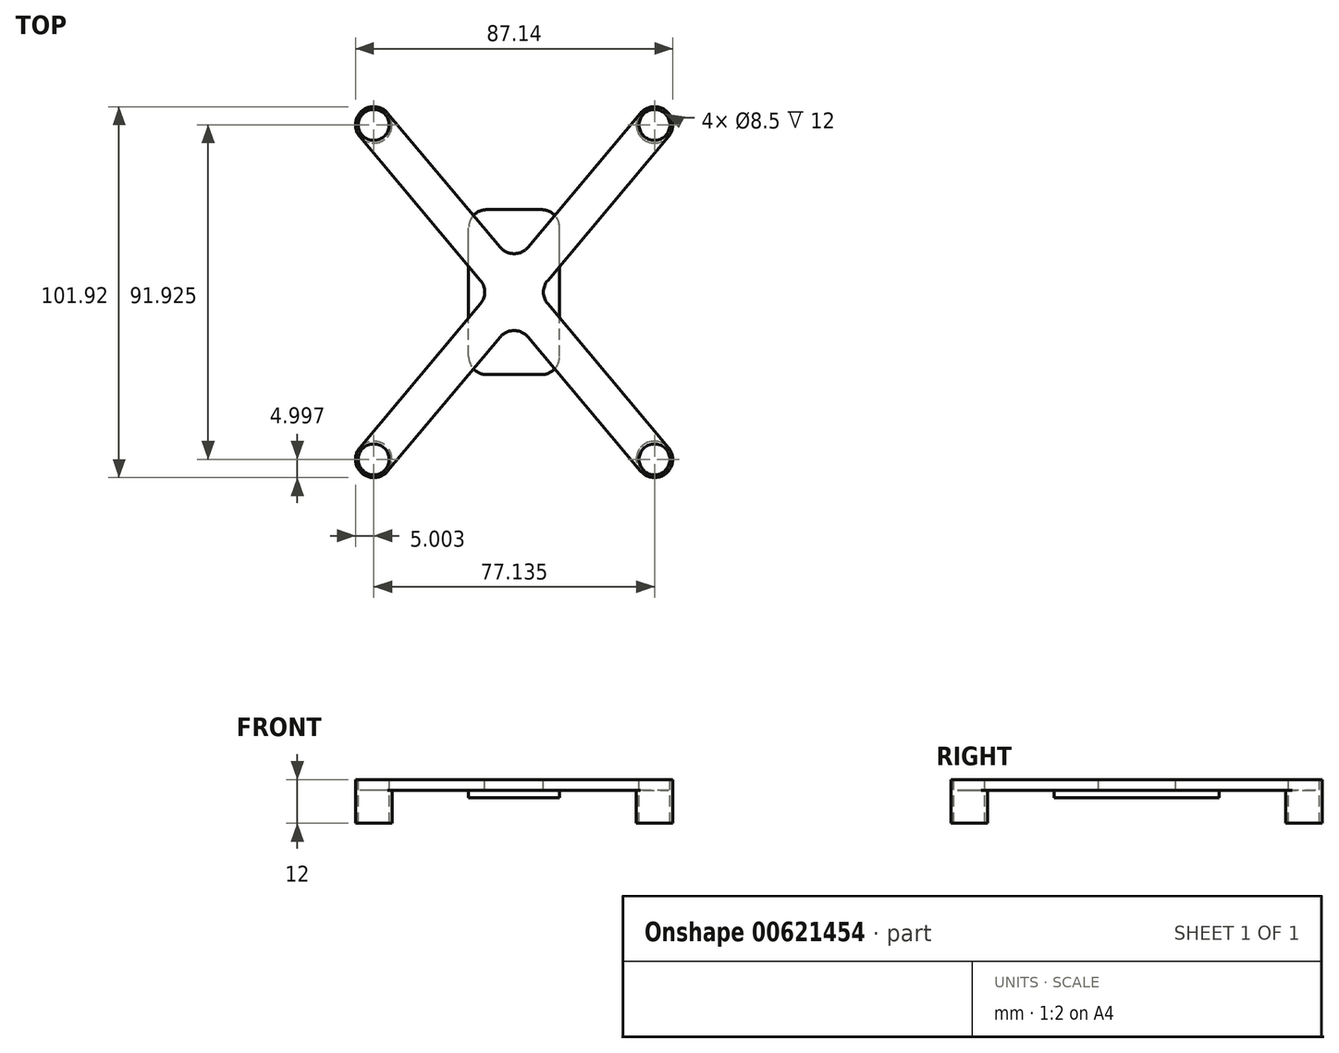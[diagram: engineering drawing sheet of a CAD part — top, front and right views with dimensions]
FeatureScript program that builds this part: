
annotation { "Feature Type Name" : "Feature", "Feature Type Description" : "" }
export const myFeature = defineFeature(function(context is Context, id is Id, definition is map)
    precondition{}
    {
        {
            var Q0;
            Q0=qCreatedBy(makeId("Top.planeOp"),FACE);
            var sketch = newSketch(context, id + "F0", { "sketchPlane" : qUnion([Q0])});
            skLineSegment(sketch, "E0.bottom", {"start": v(-42.4, 42.75) * mm, "end": v(-34.74, 49.18) * mm});
            skLineSegment(sketch, "E0.top", {"start": v(34.74, -49.18) * mm, "end": v(42.4, -42.75) * mm});
            skLineSegment(sketch, "E0.left", {"start": v(-42.4, 42.75) * mm, "end": v(-6.53, 0) * mm});
            skLineSegment(sketch, "E0.right", {"start": v(-34.74, 49.18) * mm, "end": v(0, 7.78) * mm});
            skPoint(sketch, "E0.middle", {"position": v(0, 0) * mm});
            skLineSegment(sketch, "E1.bottom", {"start": v(42.4, 42.75) * mm, "end": v(34.74, 49.18) * mm});
            skLineSegment(sketch, "E1.top", {"start": v(-34.74, -49.18) * mm, "end": v(-42.4, -42.75) * mm});
            skLineSegment(sketch, "E1.left", {"start": v(42.4, 42.75) * mm, "end": v(6.53, 0) * mm});
            skLineSegment(sketch, "E1.right", {"start": v(34.74, 49.18) * mm, "end": v(0, 7.78) * mm});
            skLineSegment(sketch, "E2.trimOffspring", {"start": v(-6.53, 0) * mm, "end": v(-42.4, -42.75) * mm});
            skLineSegment(sketch, "E3.trimOffspring", {"start": v(0, -7.78) * mm, "end": v(34.74, -49.18) * mm});
            skLineSegment(sketch, "E4.trimOffspring", {"start": v(0, -7.78) * mm, "end": v(-34.74, -49.18) * mm});
            skLineSegment(sketch, "E5.trimOffspring", {"start": v(6.53, 0) * mm, "end": v(42.4, -42.75) * mm});
            skSolve(sketch);
        }
        {
            var Q0;
            Q0=makeQuery(id+"F0.imprint","IMPRINT",FACE,{"disambiguationData":[TD([[makeQuery(id+"F0.imprint","IMPRINT",EDGE,{"derivedFrom":sQuery(id+"F0.wireOp",EDGE,"E0.bottom")}),-1.0]])]});
            extrude(context, id + "F1", {"entities" : qUnion([Q0]), "depth" : 3 * mm, "offsetDistance" : 25 * mm});
        }
        {
            var Q0;
            Q0=makeQuery(id+"F1.opExtrude","CAP_FACE",FACE,{"disambiguationData":[OSD([sQuery(id+"F0.wireOp",EDGE,"E0.bottom"),sQuery(id+"F0.wireOp",EDGE,"E0.top"),sQuery(id+"F0.wireOp",EDGE,"E0.left"),sQuery(id+"F0.wireOp",EDGE,"E0.right"),sQuery(id+"F0.wireOp",EDGE,"E1.bottom"),sQuery(id+"F0.wireOp",EDGE,"E1.top"),sQuery(id+"F0.wireOp",EDGE,"E1.left"),sQuery(id+"F0.wireOp",EDGE,"E1.right"),sQuery(id+"F0.wireOp",EDGE,"E2.trimOffspring"),sQuery(id+"F0.wireOp",EDGE,"E3.trimOffspring"),sQuery(id+"F0.wireOp",EDGE,"E4.trimOffspring"),sQuery(id+"F0.wireOp",EDGE,"E5.trimOffspring")])],"isStart":false});
            var sketch = newSketch(context, id + "F2", { "sketchPlane" : qUnion([Q0])});
            skCircle(sketch, "E6", {"center": v(-38.57, 45.96) * mm, "radius": 4.25 * mm});
            skCircle(sketch, "E7", {"center": v(-38.57, 45.96) * mm, "radius": 5 * mm});
            skCircle(sketch, "E8", {"center": v(38.57, 45.96) * mm, "radius": 5 * mm});
            skCircle(sketch, "E9", {"center": v(38.57, 45.96) * mm, "radius": 4.25 * mm});
            skCircle(sketch, "E10", {"center": v(38.57, -45.96) * mm, "radius": 5 * mm});
            skCircle(sketch, "E11", {"center": v(38.57, -45.96) * mm, "radius": 4.25 * mm});
            skCircle(sketch, "E12", {"center": v(-38.57, -45.96) * mm, "radius": 5 * mm});
            skCircle(sketch, "E13", {"center": v(-38.57, -45.96) * mm, "radius": 4.25 * mm});
            skSolve(sketch);
        }
        {
            var Q0;
            {var subQ1=makeQuery(id+"F1.opExtrude","CAP_EDGE",EDGE,{"disambiguationData":[OSD([sQuery(id+"F0.wireOp",EDGE,"E1.top")])],"isStart":false});var subQ4=sQuery(id+"F2.wireOp",EDGE,"E13");var subQ5=makeQuery(id+"F2.imprint","INTERSECT",VERTEX,{"disambiguationData":[OD(0.0)],"derivedFrom":[subQ1,subQ4]});Q0=makeQuery(id+"F2.imprint","IMPRINT",FACE,{"disambiguationData":[TD([[makeQuery(id+"F2.imprint","IMPRINT",EDGE,{"disambiguationData":[TD([[subQ5,1.0]])],"derivedFrom":subQ4}),-1.0]])]});}
            var Q1;
            {var subQ1=makeQuery(id+"F1.opExtrude","CAP_EDGE",EDGE,{"disambiguationData":[OSD([sQuery(id+"F0.wireOp",EDGE,"E1.top")])],"isStart":false});var subQ4=sQuery(id+"F2.wireOp",EDGE,"E13");var subQ5=makeQuery(id+"F2.imprint","INTERSECT",VERTEX,{"disambiguationData":[OD(0.0)],"derivedFrom":[subQ1,subQ4]});Q1=makeQuery(id+"F2.imprint","IMPRINT",FACE,{"disambiguationData":[TD([[makeQuery(id+"F2.imprint","IMPRINT",EDGE,{"disambiguationData":[TD([[subQ5,-1.0]])],"derivedFrom":subQ4}),-1.0]])]});}
            var Q2;
            {var subQ1=makeQuery(id+"F1.opExtrude","CAP_EDGE",EDGE,{"disambiguationData":[OSD([sQuery(id+"F0.wireOp",EDGE,"E0.top")])],"isStart":false});var subQ4=sQuery(id+"F2.wireOp",EDGE,"E11");var subQ5=makeQuery(id+"F2.imprint","INTERSECT",VERTEX,{"disambiguationData":[OD(0.0)],"derivedFrom":[subQ1,subQ4]});Q2=makeQuery(id+"F2.imprint","IMPRINT",FACE,{"disambiguationData":[TD([[makeQuery(id+"F2.imprint","IMPRINT",EDGE,{"disambiguationData":[TD([[subQ5,-1.0]])],"derivedFrom":subQ4}),-1.0]])]});}
            var Q3;
            {var subQ1=makeQuery(id+"F1.opExtrude","CAP_EDGE",EDGE,{"disambiguationData":[OSD([sQuery(id+"F0.wireOp",EDGE,"E0.top")])],"isStart":false});var subQ4=sQuery(id+"F2.wireOp",EDGE,"E11");var subQ6=makeQuery(id+"F2.imprint","INTERSECT",VERTEX,{"disambiguationData":[OD(0.0)],"derivedFrom":[subQ1,subQ4]});Q3=makeQuery(id+"F2.imprint","IMPRINT",FACE,{"disambiguationData":[TD([[makeQuery(id+"F2.imprint","IMPRINT",EDGE,{"disambiguationData":[TD([[subQ6,1.0]])],"derivedFrom":subQ4}),-1.0]])]});}
            var Q4;
            {var subQ0=sQuery(id+"F2.wireOp",EDGE,"E6");var subQ1=makeQuery(id+"F1.opExtrude","CAP_EDGE",EDGE,{"disambiguationData":[OSD([sQuery(id+"F0.wireOp",EDGE,"E0.bottom")])],"isStart":false});var subQ2=makeQuery(id+"F2.imprint","INTERSECT",VERTEX,{"disambiguationData":[OD(0.0)],"derivedFrom":[subQ1,subQ0]});Q4=makeQuery(id+"F2.imprint","IMPRINT",FACE,{"disambiguationData":[TD([[makeQuery(id+"F2.imprint","IMPRINT",EDGE,{"disambiguationData":[TD([[subQ2,1.0]])],"derivedFrom":subQ0}),-1.0]])]});}
            var Q5;
            {var subQ0=sQuery(id+"F2.wireOp",EDGE,"E6");var subQ1=makeQuery(id+"F1.opExtrude","CAP_EDGE",EDGE,{"disambiguationData":[OSD([sQuery(id+"F0.wireOp",EDGE,"E0.bottom")])],"isStart":false});var subQ2=makeQuery(id+"F2.imprint","INTERSECT",VERTEX,{"disambiguationData":[OD(0.0)],"derivedFrom":[subQ1,subQ0]});Q5=makeQuery(id+"F2.imprint","IMPRINT",FACE,{"disambiguationData":[TD([[makeQuery(id+"F2.imprint","IMPRINT",EDGE,{"disambiguationData":[TD([[subQ2,-1.0]])],"derivedFrom":subQ0}),-1.0]])]});}
            var Q6;
            {var subQ1=makeQuery(id+"F1.opExtrude","CAP_EDGE",EDGE,{"disambiguationData":[OSD([sQuery(id+"F0.wireOp",EDGE,"E1.bottom")])],"isStart":false});var subQ4=sQuery(id+"F2.wireOp",EDGE,"E9");var subQ5=makeQuery(id+"F2.imprint","INTERSECT",VERTEX,{"disambiguationData":[OD(0.0)],"derivedFrom":[subQ1,subQ4]});Q6=makeQuery(id+"F2.imprint","IMPRINT",FACE,{"disambiguationData":[TD([[makeQuery(id+"F2.imprint","IMPRINT",EDGE,{"disambiguationData":[TD([[subQ5,-1.0]])],"derivedFrom":subQ4}),-1.0]])]});}
            var Q7;
            {var subQ1=makeQuery(id+"F1.opExtrude","CAP_EDGE",EDGE,{"disambiguationData":[OSD([sQuery(id+"F0.wireOp",EDGE,"E1.bottom")])],"isStart":false});var subQ4=sQuery(id+"F2.wireOp",EDGE,"E9");var subQ5=makeQuery(id+"F2.imprint","INTERSECT",VERTEX,{"disambiguationData":[OD(0.0)],"derivedFrom":[subQ1,subQ4]});Q7=makeQuery(id+"F2.imprint","IMPRINT",FACE,{"disambiguationData":[TD([[makeQuery(id+"F2.imprint","IMPRINT",EDGE,{"disambiguationData":[TD([[subQ5,1.0]])],"derivedFrom":subQ4}),-1.0]])]});}
            extrude(context, id + "F3", {"entities" : qUnion([Q0, Q1, Q2, Q3, Q4, Q5, Q6, Q7]), "operationType" : NewBodyOperationType.ADD, "oppositeDirection" : true, "depth" : 12 * mm, "offsetDistance" : 25 * mm});
        }
        {
            var Q0;
            {var subQ0=sQuery(id+"F0.wireOp",EDGE,"E1.bottom");Q0=makeQuery(id+"F3.boolean.opBoolean","SPLIT",FACE,{"disambiguationData":[TD([makeQuery(id+"F1.opExtrude","SWEPT_FACE",FACE,{"disambiguationData":[OSD([subQ0])]})])],"derivedFrom":makeQuery(id+"F1.opExtrude","CAP_FACE",FACE,{"disambiguationData":[OSD([sQuery(id+"F0.wireOp",EDGE,"E0.bottom"),sQuery(id+"F0.wireOp",EDGE,"E0.top"),sQuery(id+"F0.wireOp",EDGE,"E0.left"),sQuery(id+"F0.wireOp",EDGE,"E0.right"),subQ0,sQuery(id+"F0.wireOp",EDGE,"E1.top"),sQuery(id+"F0.wireOp",EDGE,"E1.left"),sQuery(id+"F0.wireOp",EDGE,"E1.right"),sQuery(id+"F0.wireOp",EDGE,"E2.trimOffspring"),sQuery(id+"F0.wireOp",EDGE,"E3.trimOffspring"),sQuery(id+"F0.wireOp",EDGE,"E4.trimOffspring"),sQuery(id+"F0.wireOp",EDGE,"E5.trimOffspring")])],"isStart":true})});}
            var Q1;
            {var subQ0=sQuery(id+"F0.wireOp",EDGE,"E0.bottom");Q1=makeQuery(id+"F3.boolean.opBoolean","SPLIT",FACE,{"disambiguationData":[TD([makeQuery(id+"F1.opExtrude","SWEPT_FACE",FACE,{"disambiguationData":[OSD([subQ0])]})])],"derivedFrom":makeQuery(id+"F1.opExtrude","CAP_FACE",FACE,{"disambiguationData":[OSD([subQ0,sQuery(id+"F0.wireOp",EDGE,"E0.top"),sQuery(id+"F0.wireOp",EDGE,"E0.left"),sQuery(id+"F0.wireOp",EDGE,"E0.right"),sQuery(id+"F0.wireOp",EDGE,"E1.bottom"),sQuery(id+"F0.wireOp",EDGE,"E1.top"),sQuery(id+"F0.wireOp",EDGE,"E1.left"),sQuery(id+"F0.wireOp",EDGE,"E1.right"),sQuery(id+"F0.wireOp",EDGE,"E2.trimOffspring"),sQuery(id+"F0.wireOp",EDGE,"E3.trimOffspring"),sQuery(id+"F0.wireOp",EDGE,"E4.trimOffspring"),sQuery(id+"F0.wireOp",EDGE,"E5.trimOffspring")])],"isStart":true})});}
            var Q2;
            {var subQ0=sQuery(id+"F0.wireOp",EDGE,"E1.top");Q2=makeQuery(id+"F3.boolean.opBoolean","SPLIT",FACE,{"disambiguationData":[TD([makeQuery(id+"F1.opExtrude","SWEPT_FACE",FACE,{"disambiguationData":[OSD([subQ0])]})])],"derivedFrom":makeQuery(id+"F1.opExtrude","CAP_FACE",FACE,{"disambiguationData":[OSD([sQuery(id+"F0.wireOp",EDGE,"E0.bottom"),sQuery(id+"F0.wireOp",EDGE,"E0.top"),sQuery(id+"F0.wireOp",EDGE,"E0.left"),sQuery(id+"F0.wireOp",EDGE,"E0.right"),sQuery(id+"F0.wireOp",EDGE,"E1.bottom"),subQ0,sQuery(id+"F0.wireOp",EDGE,"E1.left"),sQuery(id+"F0.wireOp",EDGE,"E1.right"),sQuery(id+"F0.wireOp",EDGE,"E2.trimOffspring"),sQuery(id+"F0.wireOp",EDGE,"E3.trimOffspring"),sQuery(id+"F0.wireOp",EDGE,"E4.trimOffspring"),sQuery(id+"F0.wireOp",EDGE,"E5.trimOffspring")])],"isStart":true})});}
            var Q3;
            {var subQ0=sQuery(id+"F0.wireOp",EDGE,"E0.top");Q3=makeQuery(id+"F3.boolean.opBoolean","SPLIT",FACE,{"disambiguationData":[TD([makeQuery(id+"F1.opExtrude","SWEPT_FACE",FACE,{"disambiguationData":[OSD([subQ0])]})])],"derivedFrom":makeQuery(id+"F1.opExtrude","CAP_FACE",FACE,{"disambiguationData":[OSD([sQuery(id+"F0.wireOp",EDGE,"E0.bottom"),subQ0,sQuery(id+"F0.wireOp",EDGE,"E0.left"),sQuery(id+"F0.wireOp",EDGE,"E0.right"),sQuery(id+"F0.wireOp",EDGE,"E1.bottom"),sQuery(id+"F0.wireOp",EDGE,"E1.top"),sQuery(id+"F0.wireOp",EDGE,"E1.left"),sQuery(id+"F0.wireOp",EDGE,"E1.right"),sQuery(id+"F0.wireOp",EDGE,"E2.trimOffspring"),sQuery(id+"F0.wireOp",EDGE,"E3.trimOffspring"),sQuery(id+"F0.wireOp",EDGE,"E4.trimOffspring"),sQuery(id+"F0.wireOp",EDGE,"E5.trimOffspring")])],"isStart":true})});}
            extrude(context, id + "F4", {"entities" : qUnion([Q0, Q1, Q2, Q3]), "operationType" : NewBodyOperationType.REMOVE, "endBound" : BoundingType.THROUGH_ALL, "oppositeDirection" : true, "depth" : 25 * mm, "offsetDistance" : 25 * mm});
        }
        {
            var Q0;
            {var subQ0=sQuery(id+"F0.wireOp",EDGE,"E5.trimOffspring");var subQ1=sQuery(id+"F0.wireOp",EDGE,"E4.trimOffspring");var subQ2=sQuery(id+"F0.wireOp",EDGE,"E3.trimOffspring");var subQ3=sQuery(id+"F0.wireOp",EDGE,"E2.trimOffspring");var subQ4=sQuery(id+"F0.wireOp",EDGE,"E0.left");var subQ5=sQuery(id+"F0.wireOp",EDGE,"E1.right");var subQ6=sQuery(id+"F0.wireOp",EDGE,"E1.left");var subQ7=sQuery(id+"F0.wireOp",EDGE,"E0.right");Q0=makeQuery(id+"F3.boolean.opBoolean","SPLIT",FACE,{"disambiguationData":[TD([makeQuery(id+"F1.opExtrude","SWEPT_FACE",FACE,{"disambiguationData":[OSD([subQ4])]})])],"derivedFrom":makeQuery(id+"F1.opExtrude","CAP_FACE",FACE,{"disambiguationData":[OSD([sQuery(id+"F0.wireOp",EDGE,"E0.bottom"),sQuery(id+"F0.wireOp",EDGE,"E0.top"),subQ4,subQ7,sQuery(id+"F0.wireOp",EDGE,"E1.bottom"),sQuery(id+"F0.wireOp",EDGE,"E1.top"),subQ6,subQ5,subQ3,subQ2,subQ1,subQ0])],"isStart":true})});}
            var sketch = newSketch(context, id + "F5", { "sketchPlane" : qUnion([Q0])});
            skLineSegment(sketch, "E14.bottom", {"start": v(-12.5, 22.68) * mm, "end": v(12.5, 22.68) * mm});
            skLineSegment(sketch, "E14.top", {"start": v(-12.5, -22.68) * mm, "end": v(12.5, -22.68) * mm});
            skLineSegment(sketch, "E14.left", {"start": v(-12.5, 22.68) * mm, "end": v(-12.5, -22.68) * mm});
            skLineSegment(sketch, "E14.right", {"start": v(12.5, 22.68) * mm, "end": v(12.5, -22.68) * mm});
            skPoint(sketch, "E14.middle", {"position": v(0, 0) * mm});
            skSolve(sketch);
        }
        {
            var Q0;
            Q0 = qSketchRegion(id + "F5", true);
            extrude(context, id + "F6", {"entities" : qUnion([Q0]), "operationType" : NewBodyOperationType.ADD, "depth" : 2 * mm, "offsetDistance" : 25 * mm});
        }
        {
            var Q0;
            Q0=makeQuery(id+"F6.opExtrude","SWEPT_EDGE",EDGE,{"disambiguationData":[OSD([sQuery(id+"F0.wireOp",EDGE,"E0.right"),sQuery(id+"F5.wireOp",EDGE,"E14.top"),sQuery(id+"F5.wireOp",EDGE,"E14.left")])]});
            var Q1;
            Q1=makeQuery(id+"F6.opExtrude","SWEPT_EDGE",EDGE,{"disambiguationData":[OSD([sQuery(id+"F0.wireOp",EDGE,"E1.right"),sQuery(id+"F5.wireOp",EDGE,"E14.top"),sQuery(id+"F5.wireOp",EDGE,"E14.right")])]});
            var Q2;
            Q2=makeQuery(id+"F6.opExtrude","SWEPT_EDGE",EDGE,{"disambiguationData":[OSD([sQuery(id+"F0.wireOp",EDGE,"E4.trimOffspring"),sQuery(id+"F5.wireOp",EDGE,"E14.bottom"),sQuery(id+"F5.wireOp",EDGE,"E14.left")])]});
            var Q3;
            Q3=makeQuery(id+"F6.opExtrude","SWEPT_EDGE",EDGE,{"disambiguationData":[OSD([sQuery(id+"F0.wireOp",EDGE,"E3.trimOffspring"),sQuery(id+"F5.wireOp",EDGE,"E14.bottom"),sQuery(id+"F5.wireOp",EDGE,"E14.right")])]});
            var Q4;
            Q4=makeQuery(id+"F1.opExtrude","SWEPT_EDGE",EDGE,{"disambiguationData":[OSD([sQuery(id+"F0.wireOp",EDGE,"E0.right"),sQuery(id+"F0.wireOp",EDGE,"E1.right")])]});
            var Q5;
            Q5=makeQuery(id+"F1.opExtrude","SWEPT_EDGE",EDGE,{"disambiguationData":[OSD([sQuery(id+"F0.wireOp",EDGE,"E0.left"),sQuery(id+"F0.wireOp",EDGE,"E2.trimOffspring")])]});
            var Q6;
            Q6=makeQuery(id+"F1.opExtrude","SWEPT_EDGE",EDGE,{"disambiguationData":[OSD([sQuery(id+"F0.wireOp",EDGE,"E3.trimOffspring"),sQuery(id+"F0.wireOp",EDGE,"E4.trimOffspring")])]});
            var Q7;
            Q7=makeQuery(id+"F1.opExtrude","SWEPT_EDGE",EDGE,{"disambiguationData":[OSD([sQuery(id+"F0.wireOp",EDGE,"E1.left"),sQuery(id+"F0.wireOp",EDGE,"E5.trimOffspring")])]});
            fillet(context, id + "F7", {"entities" : qUnion([Q0, Q1, Q2, Q3, Q4, Q5, Q6, Q7]), "radius" : 5 * mm, "tangentPropagation" : true, "allowEdgeOverflow" : false});
        }
    });
